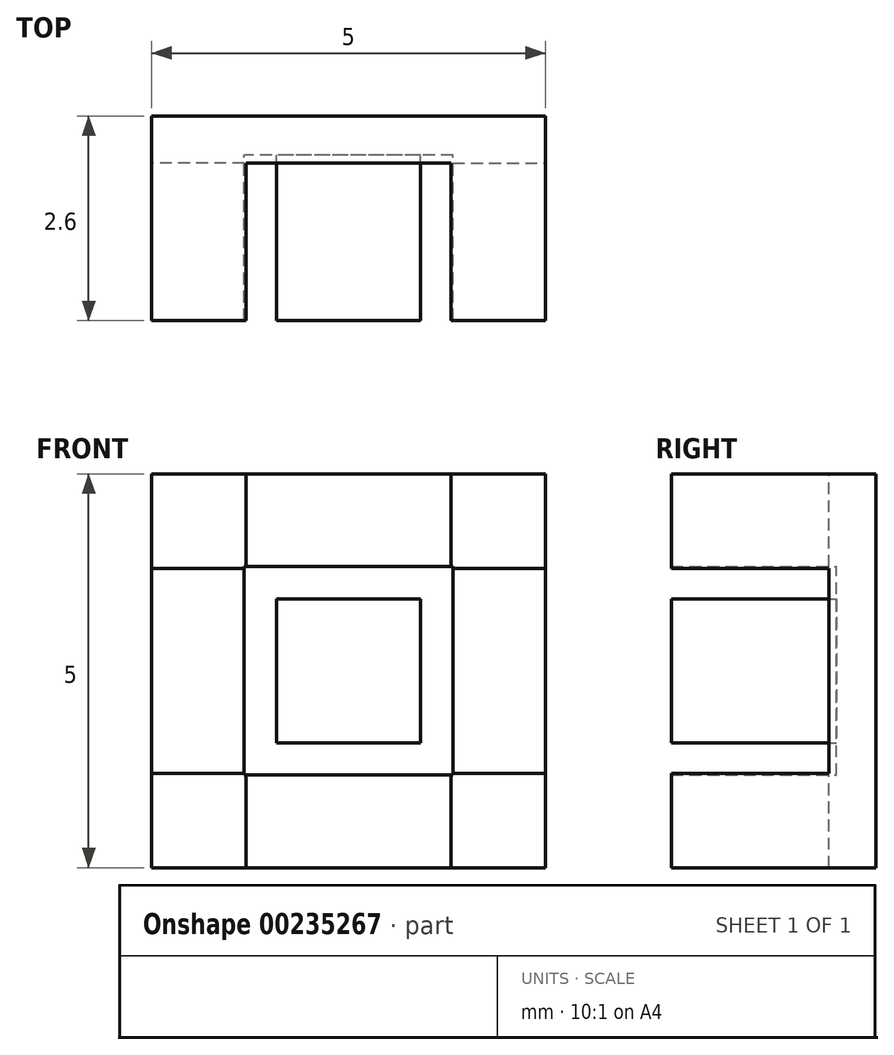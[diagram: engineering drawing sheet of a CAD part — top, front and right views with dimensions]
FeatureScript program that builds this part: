
annotation { "Feature Type Name" : "Feature", "Feature Type Description" : "" }
export const myFeature = defineFeature(function(context is Context, id is Id, definition is map)
    precondition{}
    {
        {
            var Q0;
            Q0=qCreatedBy(makeId("Front.planeOp"),FACE);
            var sketch = newSketch(context, id + "F0", { "sketchPlane" : qUnion([Q0])});
            skLineSegment(sketch, "E0.bottom", {"start": v(2.5, 2.5) * mm, "end": v(-2.5, 2.5) * mm});
            skLineSegment(sketch, "E0.top", {"start": v(2.5, -2.5) * mm, "end": v(-2.5, -2.5) * mm});
            skLineSegment(sketch, "E0.left", {"start": v(2.5, 2.5) * mm, "end": v(2.5, -2.5) * mm});
            skLineSegment(sketch, "E0.right", {"start": v(-2.5, 2.5) * mm, "end": v(-2.5, -2.5) * mm});
            skPoint(sketch, "E0.middle", {"position": v(0, 0) * mm});
            skSolve(sketch);
        }
        {
            var Q0;
            Q0 = qSketchRegion(id + "F0", true);
            extrude(context, id + "F1", {"entities" : qUnion([Q0]), "depth" : 0.5 * mm});
        }
        {
            var Q0;
            Q0=makeQuery(id+"F1.opExtrude","CAP_FACE",FACE,{"disambiguationData":[OSD([sQuery(id+"F0.wireOp",EDGE,"E0.bottom"),sQuery(id+"F0.wireOp",EDGE,"E0.top"),sQuery(id+"F0.wireOp",EDGE,"E0.left"),sQuery(id+"F0.wireOp",EDGE,"E0.right")])],"isStart":false});
            var sketch = newSketch(context, id + "F2", { "sketchPlane" : qUnion([Q0])});
            skLineSegment(sketch, "E1.bottom", {"start": v(0.91, 0.91) * mm, "end": v(-0.91, 0.91) * mm});
            skLineSegment(sketch, "E1.top", {"start": v(0.91, -0.91) * mm, "end": v(-0.91, -0.91) * mm});
            skLineSegment(sketch, "E1.left", {"start": v(0.91, 0.91) * mm, "end": v(0.91, -0.91) * mm});
            skLineSegment(sketch, "E1.right", {"start": v(-0.91, 0.91) * mm, "end": v(-0.91, -0.91) * mm});
            skPoint(sketch, "E1.middle", {"position": v(0, 0) * mm});
            skSolve(sketch);
        }
        {
            var Q0;
            Q0 = qSketchRegion(id + "F2", true);
            extrude(context, id + "F3", {"entities" : qUnion([Q0]), "operationType" : NewBodyOperationType.ADD, "depth" : 2.1 * mm});
        }
        {
            var Q0;
            Q0=makeQuery(id+"F1.opExtrude","CAP_FACE",FACE,{"disambiguationData":[OSD([sQuery(id+"F0.wireOp",EDGE,"E0.bottom"),sQuery(id+"F0.wireOp",EDGE,"E0.top"),sQuery(id+"F0.wireOp",EDGE,"E0.left"),sQuery(id+"F0.wireOp",EDGE,"E0.right")])],"isStart":false});
            var sketch = newSketch(context, id + "F4", { "sketchPlane" : qUnion([Q0])});
            skLineSegment(sketch, "E2", {"start": v(-2.5, -2.5) * mm, "end": v(-1.3, -2.5) * mm});
            skLineSegment(sketch, "E3", {"start": v(-1.3, -2.5) * mm, "end": v(-1.3, -1.32) * mm});
            skLineSegment(sketch, "E4", {"start": v(-1.3, -1.32) * mm, "end": v(-1.33, -1.32) * mm});
            skLineSegment(sketch, "E5", {"start": v(-1.33, -1.32) * mm, "end": v(-1.33, -1.3) * mm});
            skLineSegment(sketch, "E6", {"start": v(-1.33, -1.3) * mm, "end": v(-2.5, -1.3) * mm});
            skLineSegment(sketch, "E7", {"start": v(-2.5, -1.3) * mm, "end": v(-2.5, -2.5) * mm});
            skSolve(sketch);
        }
        {
            var Q0;
            Q0 = qSketchRegion(id + "F4", true);
            extrude(context, id + "F5", {"entities" : qUnion([Q0]), "operationType" : NewBodyOperationType.ADD, "depth" : 2.1 * mm});
        }
        {
            var Q0;
            Q0=makeQuery(id+"F1.opExtrude","CAP_FACE",FACE,{"disambiguationData":[OSD([sQuery(id+"F0.wireOp",EDGE,"E0.bottom"),sQuery(id+"F0.wireOp",EDGE,"E0.top"),sQuery(id+"F0.wireOp",EDGE,"E0.left"),sQuery(id+"F0.wireOp",EDGE,"E0.right")])],"isStart":false});
            var sketch = newSketch(context, id + "F6", { "sketchPlane" : qUnion([Q0])});
            skLineSegment(sketch, "E8.bottom", {"start": v(-1.3, -2.5) * mm, "end": v(1.3, -2.5) * mm});
            skLineSegment(sketch, "E8.top", {"start": v(-1.3, -1.32) * mm, "end": v(1.3, -1.32) * mm});
            skLineSegment(sketch, "E8.left", {"start": v(-1.3, -2.5) * mm, "end": v(-1.3, -1.32) * mm});
            skLineSegment(sketch, "E8.right", {"start": v(1.3, -2.5) * mm, "end": v(1.3, -1.32) * mm});
            skSolve(sketch);
        }
        {
            var Q0;
            Q0 = qSketchRegion(id + "F6", true);
            extrude(context, id + "F7", {"entities" : qUnion([Q0]), "operationType" : NewBodyOperationType.ADD, "depth" : .1 * mm});
        }
        {
            var Q0;
            Q0=makeQuery(id+"F1.opExtrude","CAP_FACE",FACE,{"disambiguationData":[OSD([sQuery(id+"F0.wireOp",EDGE,"E0.bottom"),sQuery(id+"F0.wireOp",EDGE,"E0.top"),sQuery(id+"F0.wireOp",EDGE,"E0.left"),sQuery(id+"F0.wireOp",EDGE,"E0.right")])],"isStart":false});
            var sketch = newSketch(context, id + "F8", { "sketchPlane" : qUnion([Q0])});
            skLineSegment(sketch, "E9", {"start": v(1.3, -2.5) * mm, "end": v(1.3, -1.32) * mm});
            skLineSegment(sketch, "E10", {"start": v(1.3, -1.32) * mm, "end": v(1.32, -1.32) * mm});
            skLineSegment(sketch, "E11", {"start": v(1.32, -1.32) * mm, "end": v(1.32, -1.3) * mm});
            skLineSegment(sketch, "E12", {"start": v(1.32, -1.3) * mm, "end": v(2.5, -1.3) * mm});
            skLineSegment(sketch, "E13", {"start": v(2.5, -1.3) * mm, "end": v(2.5, -2.5) * mm});
            skLineSegment(sketch, "E14", {"start": v(2.5, -2.5) * mm, "end": v(1.3, -2.5) * mm});
            skSolve(sketch);
        }
        {
            var Q0;
            Q0 = qSketchRegion(id + "F8", true);
            extrude(context, id + "F9", {"entities" : qUnion([Q0]), "operationType" : NewBodyOperationType.ADD, "depth" : 2.1 * mm});
        }
        {
            var Q0;
            Q0=makeQuery(id+"F1.opExtrude","CAP_FACE",FACE,{"disambiguationData":[OSD([sQuery(id+"F0.wireOp",EDGE,"E0.bottom"),sQuery(id+"F0.wireOp",EDGE,"E0.top"),sQuery(id+"F0.wireOp",EDGE,"E0.left"),sQuery(id+"F0.wireOp",EDGE,"E0.right")])],"isStart":false});
            var sketch = newSketch(context, id + "F10", { "sketchPlane" : qUnion([Q0])});
            skLineSegment(sketch, "E15.bottom", {"start": v(1.32, -1.3) * mm, "end": v(2.5, -1.3) * mm});
            skLineSegment(sketch, "E15.top", {"start": v(1.32, 1.3) * mm, "end": v(2.5, 1.3) * mm});
            skLineSegment(sketch, "E15.left", {"start": v(1.32, -1.3) * mm, "end": v(1.32, 1.3) * mm});
            skLineSegment(sketch, "E15.right", {"start": v(2.5, -1.3) * mm, "end": v(2.5, 1.3) * mm});
            skSolve(sketch);
        }
        {
            var Q0;
            Q0 = qSketchRegion(id + "F10", true);
            extrude(context, id + "F11", {"entities" : qUnion([Q0]), "operationType" : NewBodyOperationType.ADD, "depth" : 0.1 * mm});
        }
        {
            var Q0;
            Q0=makeQuery(id+"F1.opExtrude","CAP_FACE",FACE,{"disambiguationData":[OSD([sQuery(id+"F0.wireOp",EDGE,"E0.bottom"),sQuery(id+"F0.wireOp",EDGE,"E0.top"),sQuery(id+"F0.wireOp",EDGE,"E0.left"),sQuery(id+"F0.wireOp",EDGE,"E0.right")])],"isStart":false});
            var sketch = newSketch(context, id + "F12", { "sketchPlane" : qUnion([Q0])});
            skLineSegment(sketch, "E16", {"start": v(1.32, 1.3) * mm, "end": v(1.32, 1.33) * mm});
            skLineSegment(sketch, "E17", {"start": v(1.32, 1.33) * mm, "end": v(1.3, 1.33) * mm});
            skLineSegment(sketch, "E18", {"start": v(1.3, 1.33) * mm, "end": v(1.3, 2.5) * mm});
            skLineSegment(sketch, "E19", {"start": v(1.3, 2.5) * mm, "end": v(2.5, 2.5) * mm});
            skLineSegment(sketch, "E20", {"start": v(2.5, 2.5) * mm, "end": v(2.5, 1.3) * mm});
            skLineSegment(sketch, "E21", {"start": v(1.32, 1.3) * mm, "end": v(2.5, 1.3) * mm});
            skSolve(sketch);
        }
        {
            var Q0;
            Q0 = qSketchRegion(id + "F12", true);
            extrude(context, id + "F13", {"entities" : qUnion([Q0]), "operationType" : NewBodyOperationType.ADD, "depth" : 2.1 * mm});
        }
        {
            var Q0;
            Q0=makeQuery(id+"F1.opExtrude","CAP_FACE",FACE,{"disambiguationData":[OSD([sQuery(id+"F0.wireOp",EDGE,"E0.bottom"),sQuery(id+"F0.wireOp",EDGE,"E0.top"),sQuery(id+"F0.wireOp",EDGE,"E0.left"),sQuery(id+"F0.wireOp",EDGE,"E0.right")])],"isStart":false});
            var sketch = newSketch(context, id + "F14", { "sketchPlane" : qUnion([Q0])});
            skLineSegment(sketch, "E22.bottom", {"start": v(1.3, 1.33) * mm, "end": v(-1.3, 1.33) * mm});
            skLineSegment(sketch, "E22.top", {"start": v(1.3, 2.5) * mm, "end": v(-1.3, 2.5) * mm});
            skLineSegment(sketch, "E22.left", {"start": v(1.3, 1.33) * mm, "end": v(1.3, 2.5) * mm});
            skLineSegment(sketch, "E22.right", {"start": v(-1.3, 1.33) * mm, "end": v(-1.3, 2.5) * mm});
            skSolve(sketch);
        }
        {
            var Q0;
            Q0 = qSketchRegion(id + "F14", true);
            extrude(context, id + "F15", {"entities" : qUnion([Q0]), "operationType" : NewBodyOperationType.ADD, "depth" : 0.1 * mm});
        }
        {
            var Q0;
            Q0=makeQuery(id+"F1.opExtrude","CAP_FACE",FACE,{"disambiguationData":[OSD([sQuery(id+"F0.wireOp",EDGE,"E0.bottom"),sQuery(id+"F0.wireOp",EDGE,"E0.top"),sQuery(id+"F0.wireOp",EDGE,"E0.left"),sQuery(id+"F0.wireOp",EDGE,"E0.right")])],"isStart":false});
            var sketch = newSketch(context, id + "F16", { "sketchPlane" : qUnion([Q0])});
            skLineSegment(sketch, "E23", {"start": v(-1.3, 2.5) * mm, "end": v(-1.3, 1.33) * mm});
            skLineSegment(sketch, "E24", {"start": v(-1.3, 1.33) * mm, "end": v(-1.33, 1.33) * mm});
            skLineSegment(sketch, "E25", {"start": v(-1.33, 1.33) * mm, "end": v(-1.33, 1.3) * mm});
            skLineSegment(sketch, "E26", {"start": v(-1.33, 1.3) * mm, "end": v(-2.5, 1.3) * mm});
            skLineSegment(sketch, "E27", {"start": v(-2.5, 1.3) * mm, "end": v(-2.5, 2.5) * mm});
            skLineSegment(sketch, "E28", {"start": v(-2.5, 2.5) * mm, "end": v(-1.3, 2.5) * mm});
            skSolve(sketch);
        }
        {
            var Q0;
            Q0 = qSketchRegion(id + "F16", true);
            extrude(context, id + "F17", {"entities" : qUnion([Q0]), "operationType" : NewBodyOperationType.ADD, "depth" : 2.1 * mm});
        }
        {
            var Q0;
            Q0=makeQuery(id+"F1.opExtrude","CAP_FACE",FACE,{"disambiguationData":[OSD([sQuery(id+"F0.wireOp",EDGE,"E0.bottom"),sQuery(id+"F0.wireOp",EDGE,"E0.top"),sQuery(id+"F0.wireOp",EDGE,"E0.left"),sQuery(id+"F0.wireOp",EDGE,"E0.right")])],"isStart":false});
            var sketch = newSketch(context, id + "F18", { "sketchPlane" : qUnion([Q0])});
            skLineSegment(sketch, "E29.bottom", {"start": v(-1.33, 1.3) * mm, "end": v(-2.5, 1.3) * mm});
            skLineSegment(sketch, "E29.top", {"start": v(-1.33, -1.3) * mm, "end": v(-2.5, -1.3) * mm});
            skLineSegment(sketch, "E29.left", {"start": v(-1.33, 1.3) * mm, "end": v(-1.33, -1.3) * mm});
            skLineSegment(sketch, "E29.right", {"start": v(-2.5, 1.3) * mm, "end": v(-2.5, -1.3) * mm});
            skSolve(sketch);
        }
        {
            var Q0;
            Q0 = qSketchRegion(id + "F18", true);
            extrude(context, id + "F19", {"entities" : qUnion([Q0]), "operationType" : NewBodyOperationType.ADD, "depth" : 0.1 * mm});
        }
    });
